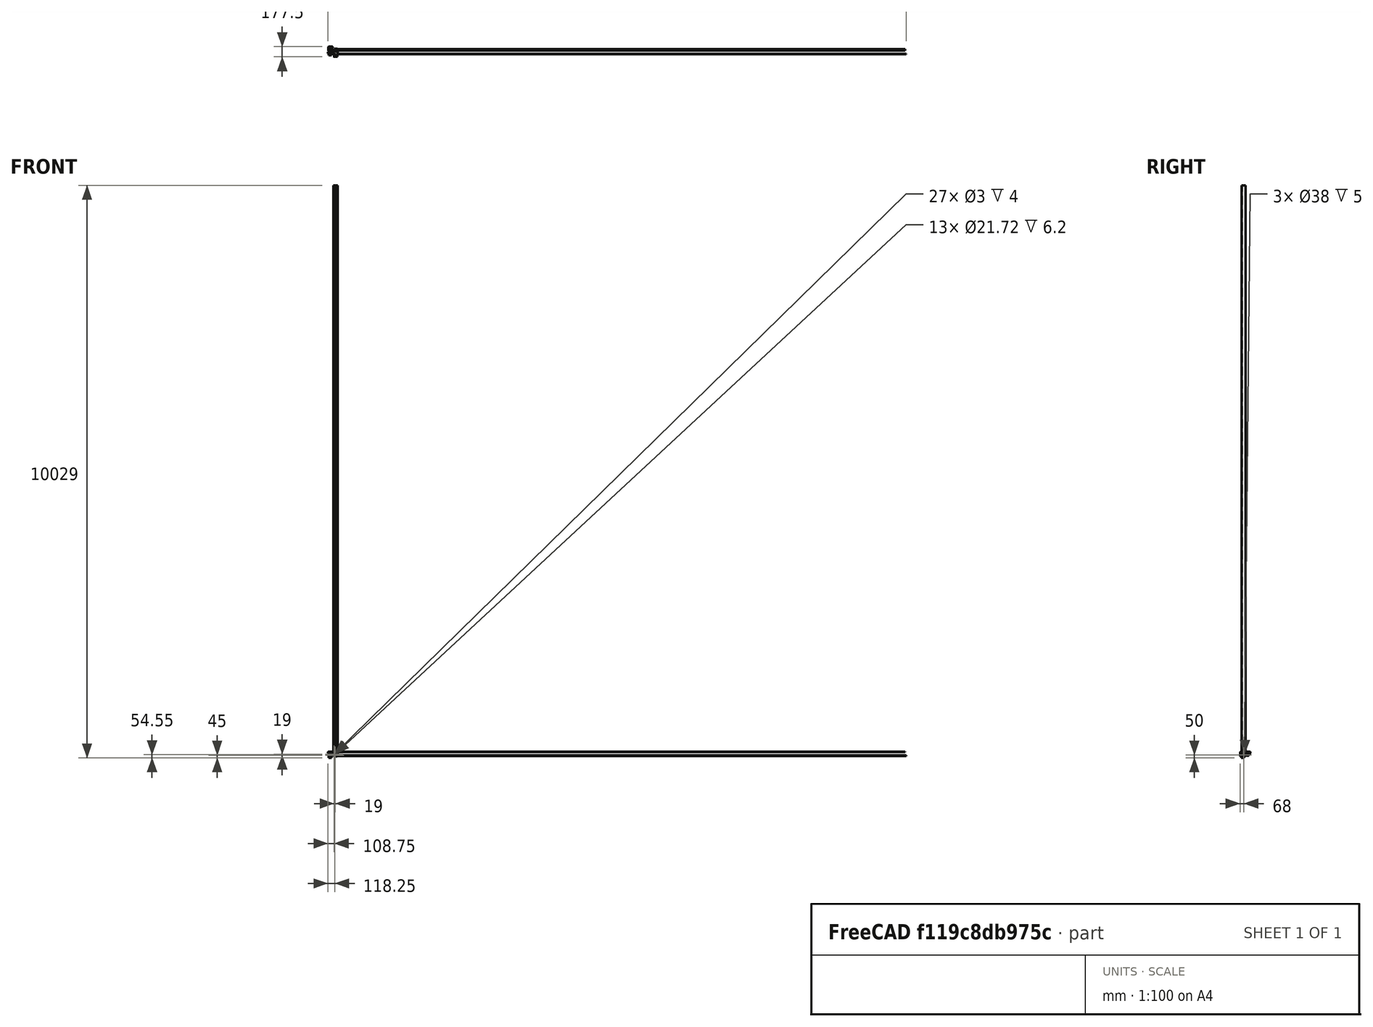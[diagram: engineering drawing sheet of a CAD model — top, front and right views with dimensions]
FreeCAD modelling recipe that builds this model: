
FCSTD DOCUMENT  (FreeCAD 0.15R4671 (Git))
Label: AllMetalJheadHotendFanShroud
License: All rights reserved
LicenseURL: http://en.wikipedia.org/wiki/All_rights_reserved
objects: Sketcher::SketchObject×30, Part::Feature×23, Mesh::Feature×22, PartDesign::Pocket×18, PartDesign::Pad×12, PartDesign::Fillet×10, Part::MultiFuse×1, PartDesign::Chamfer×1
note: 125 computed .brp shape members not serialized (recipe doc carries the construction recipe); baked Part::Feature solids carry a one-line shape summary decoded from their .brp

FEATURE [Part::Feature] Part__Feature  label="OB1515_45mm001"
  Placement = pos=(0,79.5,22.5) rot=(1,0,0;1.5708rad)
  shape: bbox 15 x 45 x 15 mm, 158 faces (baked)
FEATURE [Part::Feature] Part__Feature001  label="OB1515_45mm"
  Placement = pos=(7,93,-15) rot=(0,0,1;0.785398rad)
  shape: bbox 21.01 x 21.01 x 45 mm, 158 faces (baked)
FEATURE [Part::Feature] Part__Feature002  label="OB1515_45mm002"
  Placement = pos=(20.5,100,22.5) rot=(0.57735,0.57735,0.57735;2.0944rad)
  shape: bbox 45 x 15 x 15 mm, 158 faces (baked)
FEATURE [Part::Feature] Part__Feature003  label="NEMA17"
  Placement = pos=(36,64,2) rot=(0,0,1;0rad)
  shape: bbox 42.3 x 42.3 x 68 mm, 275 faces (baked)
FEATURE [Part::Feature] Part__Feature004  label="T5_Pulley"
  Placement = pos=(36,64,-4) rot=(0,0,1;0rad)
  shape: bbox 16 x 16 x 14.8 mm, 116 faces (baked)
FEATURE [Mesh::Feature] _08ZZ_Ball_Bearing  label="608ZZ_Ball_Bearing001"
  Placement = pos=(54.5,64,25.1) rot=(0,0,1;0rad)
FEATURE [Mesh::Feature] Spacer
  Placement = pos=(21.5,54,17.6) rot=(0,0,1;0rad)
FEATURE [Mesh::Feature] _mmRod_x100mm  label="8mmRod_x100mm"
  Placement = pos=(36,-64.5,-3.5) rot=(0,0,1;3.14159rad)
FEATURE [Part::Feature] Part__Feature005  label="TopCornerMotor"
  Placement = pos=(0,100,0) rot=(0,0,1;0rad)
  shape: bbox 69.55 x 77 x 28 mm, 82 faces (baked)
FEATURE [Part::Feature] Part__Feature006  label="TopRodHolder"
  Placement = pos=(0,100,2) rot=(0,0,1;0rad)
  shape: bbox 30.16 x 11.33 x 11.99 mm, 58 faces (baked)
FEATURE [Part::Feature] LM8UU_8mm_Linear_Bearing001
  Placement = pos=(36,-24.5,-3.5) rot=(0,0,1;1.5708rad)
  shape: bbox 15 x 24 x 15 mm, 34 faces (baked)
FEATURE [Mesh::Feature] _mmRod_x100mm001  label="8mmRod_x100mm001"
  Placement = pos=(66,7.5,1.5) rot=(0,0,1;1.5708rad)
FEATURE [Mesh::Feature] _mmRod_x100mm002  label="8mmRod_x100mm002"
  Placement = pos=(66,-32.5,1.5) rot=(0,0,1;1.5708rad)
FEATURE [Mesh::Feature] _0mmFan  label="40mmFan"
  Placement = pos=(102,-18,-36) rot=(-1,0,0;1.5708rad)
FEATURE [Mesh::Feature] HexHotEnd  label="HexHotEnd1"
  Placement = pos=(104,-57,-34) rot=(0,0,1;0rad)
FEATURE [Mesh::Feature] PNEUMATIC_NIPPLE
  Placement = pos=(111,-66,-3) rot=(0,-1,0;1.5708rad)
FEATURE [Part::Feature] Part__Feature015  label="AluAngle"
  Placement = pos=(0,5,-80) rot=(-1,0,0;1.5708rad)
  shape: bbox 50 x 50.8 x 50.8 mm, 9 faces (baked)
FEATURE [Mesh::Feature] _x10x4_FlangedBearing  label="5x10x4_FlangedBearing_BOTTOM"
  Placement = pos=(49,-6,16) rot=(-1,0,0;1.5708rad)
FEATURE [Mesh::Feature] _x10x4_FlangedBearing001  label="5x10x4_FlangedBearing_TOP"
  Placement = pos=(49,-6,12) rot=(1,0,0;1.5708rad)
FEATURE [Mesh::Feature] _x10x4_FlangedBearing002  label="5x10x4_FlangedBearing_BOTTOM001"
  Placement = pos=(49,-19,16) rot=(-1,0,0;1.5708rad)
FEATURE [Mesh::Feature] _x10x4_FlangedBearing003  label="5x10x4_FlangedBearing_TOP001"
  Placement = pos=(49,-19,12) rot=(1,0,0;1.5708rad)
FEATURE [Part::Feature] Part__Feature016  label="XCarrageBeltBlock"
  Placement = pos=(9,0,0) rot=(0,0,1;0rad)
  shape: bbox 56 x 22 x 10 mm, 113 faces (baked)
FEATURE [Part::Feature] Part__Feature017  label="LJ18A3"
  Placement = pos=(136,-57,-52) rot=(0,0,1;0rad)
  shape: bbox 17.85 x 17.85 x 79.1 mm, 11 faces (baked)
FEATURE [Mesh::Feature] HexNutStyle1_M002  label="HexNutStyle1_M006"
  Placement = pos=(50.3,7.15,-114) rot=(0,0,1;0.523599rad)
FEATURE [Mesh::Feature] HexNutStyle1_M003  label="HexNutStyle1_M007"
  Placement = pos=(50.3,20.15,-114) rot=(0,0,1;0.523599rad)
FEATURE [Part::Feature] Part__Feature018  label="YCarrage"
  shape: bbox 34.23 x 25.99 x 62.01 mm, 85 faces (baked)
FEATURE [Part::Feature] LM8UU_8mm_Linear_Bearing
  Placement = pos=(95,7.5,1.5) rot=(-1,0,0;1.5708rad)
  shape: bbox 24 x 15 x 15 mm, 34 faces (baked)
FEATURE [Part::Feature] LM8UU_8mm_Linear_Bearing002
  Placement = pos=(95,-32.5,1.5) rot=(-1,0,0;1.5708rad)
  shape: bbox 24 x 15 x 15 mm, 34 faces (baked)
FEATURE [Part::Feature] LM8UU_8mm_Linear_Bearing003
  Placement = pos=(123,7.5,1.5) rot=(-1,0,0;1.5708rad)
  shape: bbox 24 x 15 x 15 mm, 34 faces (baked)
FEATURE [Part::Feature] LM8UU_8mm_Linear_Bearing004
  Placement = pos=(123,-32.5,1.5) rot=(-1,0,0;1.5708rad)
  shape: bbox 24 x 15 x 15 mm, 34 faces (baked)
FEATURE [Mesh::Feature] MicroSwitch
  Placement = pos=(99,-12.5,-5) rot=(0,0,1;1.5708rad)
FEATURE [Part::Feature] Part__Feature019  label="XCarrageTop"
  shape: bbox 56 x 70.62 x 16.52 mm, 278 faces (baked)
FEATURE [Part::Feature] Part__Feature020  label="ChinaBlowerFan"
  shape: bbox 33.55 x 33.55 x 13 mm, 169 faces (baked)
FEATURE [Part::Feature] Part__Feature021  label="ChinaBlowerFan001"
  shape: bbox 40.62 x 40.6 x 19.6 mm, 81 faces (baked)
FEATURE [Part::MultiFuse] Fusion  label="ChinaBlowerFan002"
  Placement = pos=(114,-4,-13) rot=(0.707107,0.707107,0;3.14159rad)
  Shapes = -> [Part__Feature020,Part__Feature021]
FEATURE [Mesh::Feature] _0mmFan001  label="40mmFan001"
  Placement = pos=(141,-1,-23) rot=(0.57735,-0.57735,0.57735;4.18879rad)
FEATURE [Mesh::Feature] ALIEXPRESS_Aluhotend40mmFan
FEATURE [Mesh::Feature] Fan_25mm_x_10mm
  Placement = pos=(105.5,-31,-25.5) rot=(0,0.707107,0.707107;3.14159rad)
FEATURE [Mesh::Feature] HexHotEnd2
  Placement = pos=(104,-57,-34) rot=(0,0,1;0rad)
FEATURE [Part::Feature] Part__Feature022  label="Hexagon fanshroud"
  shape: bbox 25.5 x 25.5 x 18 mm, 35 faces (baked)
FEATURE [Mesh::Feature] hexagon_fan
  Placement = pos=(198.15,-46.7,56) rot=(0.57735,-0.57735,0.57735;2.0944rad)
FEATURE [Part::Feature] Part__Feature023  label="TempXCarrageBottom"
  shape: bbox 57.67 x 88 x 16.5 mm, 58 faces (baked)
FEATURE [Sketcher::SketchObject] Sketch
  Placement = pos=(0,0,-10.2) rot=(1,0,0;3.14159rad)
  sketch-geometry (4):
    g0: LineSegment StartX=93 StartY=70 StartZ=0 EndX=149 EndY=70 EndZ=0
    g1: LineSegment StartX=149 StartY=70 StartZ=0 EndX=149 EndY=-18 EndZ=0
    g2: LineSegment StartX=149 StartY=-18 StartZ=0 EndX=93 EndY=-18 EndZ=0
    g3: LineSegment StartX=93 StartY=-18 StartZ=0 EndX=93 EndY=70 EndZ=0
  constraints (8):
    c: Coincident(g0,g1)
    c: Coincident(g1,g2)
    c: Coincident(g2,g3)
    c: Coincident(g3,g0)
    c: Horizontal(g0)
    c: Horizontal(g2)
    c: Vertical(g1)
    c: Vertical(g3)
FEATURE [PartDesign::Pad] Pad
  Length = 3
  Length2 = 100
  Placement = pos=(0,0,-10.2) rot=(1,0,0;3.14159rad)
  Sketch = -> Sketch
  Type = 0
FEATURE [Sketcher::SketchObject] Sketch001
  Placement = pos=(0,0,-13.2) rot=(1,0,0;3.14159rad)
  Support = -> Pad [Face6]
  sketch-geometry (11):
    g0: LineSegment StartX=93 StartY=36 StartZ=0 EndX=118 EndY=36 EndZ=0
    g1: LineSegment StartX=118 StartY=36 StartZ=0 EndX=118 EndY=41 EndZ=0
    g2: LineSegment StartX=118 StartY=41 StartZ=0 EndX=114.5 EndY=62 EndZ=0
    g3: LineSegment StartX=93.5 StartY=62 StartZ=0 EndX=93 EndY=41 EndZ=0
    g4: LineSegment StartX=93 StartY=41 StartZ=0 EndX=93 EndY=36 EndZ=0
    g5: LineSegment StartX=114.5 StartY=62 StartZ=0 EndX=113 EndY=62 EndZ=0
    g6: LineSegment StartX=113 StartY=62 StartZ=0 EndX=113 EndY=52 EndZ=0
    g7: LineSegment StartX=113 StartY=52 StartZ=0 EndX=104 EndY=47 EndZ=0
    g8: LineSegment StartX=104 StartY=47 StartZ=0 EndX=95 EndY=52 EndZ=0
    g9: LineSegment StartX=95 StartY=52 StartZ=0 EndX=95 EndY=62 EndZ=0
    g10: LineSegment StartX=95 StartY=62 StartZ=0 EndX=93.5 EndY=62 EndZ=0
  constraints (16):
    c: Horizontal(g0)
    c: Coincident(g0,g1)
    c: Coincident(g1,g2)
    c: Coincident(g3,g4)
    c: Coincident(g4,g0)
    c: Coincident(g2,g5)
    c: Horizontal(g5)
    c: Coincident(g5,g6)
    c: Vertical(g6)
    c: Coincident(g6,g7)
    c: Coincident(g7,g8)
    c: Coincident(g8,g9)
    c: Vertical(g9)
    c: Coincident(g9,g10)
    c: Coincident(g10,g3)
    c: Horizontal(g10)
FEATURE [PartDesign::Pad] Pad001
  Length = 24.5
  Length2 = 100
  Placement = pos=(0,0,-10.2) rot=(1,0,0;3.14159rad)
  Sketch = -> Sketch001
  Type = 0
FEATURE [Sketcher::SketchObject] Sketch002
  Placement = pos=(93,0,-10.2) rot=(0.57735,0.57735,-0.57735;4.18879rad)
  Support = -> Pad001 [Face17]
  sketch-geometry (6):
    g0: LineSegment StartX=-63 StartY=23.5 StartZ=0 EndX=-62 EndY=23.5 EndZ=0
    g1: LineSegment StartX=-62 StartY=23.5 StartZ=0 EndX=-47 EndY=23.5 EndZ=0
    g2: LineSegment StartX=-47 StartY=23.5 StartZ=0 EndX=-41 EndY=25.5 EndZ=0
    g3: LineSegment StartX=-41 StartY=25.5 StartZ=0 EndX=-41 EndY=28 EndZ=0
    g4: LineSegment StartX=-41 StartY=28 StartZ=0 EndX=-63 EndY=28 EndZ=0
    g5: LineSegment StartX=-63 StartY=28 StartZ=0 EndX=-63 EndY=23.5 EndZ=0
  constraints (11):
    c: Horizontal(g0)
    c: Coincident(g0,g1)
    c: Horizontal(g1)
    c: Coincident(g1,g2)
    c: Coincident(g2,g3)
    c: Vertical(g3)
    c: Coincident(g3,g4)
    c: Horizontal(g4)
    c: Coincident(g4,g5)
    c: Coincident(g5,g0)
    c: Vertical(g5)
FEATURE [PartDesign::Pocket] Pocket
  Length = 5
  Placement = pos=(0,0,-10.2) rot=(1,0,0;3.14159rad)
  Sketch = -> Sketch002
  Type = 1
FEATURE [Sketcher::SketchObject] Sketch003
  Placement = pos=(0,-36,-10.2) rot=(-1,0,0;1.5708rad)
  Support = -> Pocket [Face7]
  sketch-geometry (1):
    g0: Circle CenterX=105.5 CenterY=15.25 CenterZ=0 NormalX=0 NormalY=0 NormalZ=1 Radius=10.8605
FEATURE [PartDesign::Pocket] Pocket001
  Length = 3
  Placement = pos=(0,0,-10.2) rot=(1,0,0;3.14159rad)
  Sketch = -> Sketch003
  Type = 0
FEATURE [Sketcher::SketchObject] Sketch004
  Placement = pos=(0,0,-10.2) rot=(0,0,1;0rad)
  Support = -> Pocket001 [Face4]
  sketch-geometry (7):
    g0: LineSegment StartX=94.75 StartY=-70.5 StartZ=0 EndX=94.75 EndY=-38.75 EndZ=0
    g1: LineSegment StartX=94.75 StartY=-38.75 StartZ=0 EndX=116.25 EndY=-38.75 EndZ=0
    g2: LineSegment StartX=116.25 StartY=-38.75 StartZ=0 EndX=116.5 EndY=-39 EndZ=0
    g3: LineSegment StartX=116.5 StartY=-39 StartZ=0 EndX=116.5 EndY=-41 EndZ=0
    g4: LineSegment StartX=116.5 StartY=-41 StartZ=0 EndX=113 EndY=-62 EndZ=0
    g5: LineSegment StartX=113 StartY=-62 StartZ=0 EndX=113 EndY=-70.5 EndZ=0
    g6: LineSegment StartX=113 StartY=-70.5 StartZ=0 EndX=94.75 EndY=-70.5 EndZ=0
  constraints (12):
    c: Vertical(g0)
    c: Horizontal(g1)
    c: Coincident(g1,g2)
    c: Coincident(g2,g3)
    c: Vertical(g3)
    c: Coincident(g3,g4)
    c: Coincident(g4,g5)
    c: Vertical(g5)
    c: Coincident(g5,g6)
    c: Horizontal(g6)
    c: Coincident(g0,g6)
    c: Coincident(g0,g1)
FEATURE [PartDesign::Pocket] Pocket002
  Length = 22.8
  Placement = pos=(0,0,-10.2) rot=(1,0,0;3.14159rad)
  Sketch = -> Sketch004
  Type = 0
FEATURE [PartDesign::Chamfer] Chamfer
  Base = -> Pocket002 [Edge60]
  Placement = pos=(0,0,-10.2) rot=(1,0,0;3.14159rad)
  Size = 3.2
FEATURE [PartDesign::Fillet] Fillet
  Base = -> Chamfer [Edge86,Edge76]
  Placement = pos=(0,0,-10.2) rot=(1,0,0;3.14159rad)
  Radius = 2
FEATURE [Sketcher::SketchObject] Sketch005
  Placement = pos=(0,0,-13.2) rot=(1,0,0;3.14159rad)
  Support = -> Fillet [Face4]
  sketch-geometry (8):
    g0: LineSegment StartX=92.5 StartY=41 StartZ=0 EndX=93.5 EndY=41 EndZ=0
    g1: LineSegment StartX=93.5 StartY=41 StartZ=0 EndX=93.5 EndY=62 EndZ=0
    g2: LineSegment StartX=93.5 StartY=62 StartZ=0 EndX=114.5 EndY=62 EndZ=0
    g3: LineSegment StartX=114.5 StartY=62 StartZ=0 EndX=118 EndY=41 EndZ=0
    g4: LineSegment StartX=118 StartY=41 StartZ=0 EndX=149.5 EndY=41 EndZ=0
    g5: LineSegment StartX=149.5 StartY=41 StartZ=0 EndX=149.5 EndY=70.25 EndZ=0
    g6: LineSegment StartX=149.5 StartY=70.25 StartZ=0 EndX=92.5 EndY=70.25 EndZ=0
    g7: LineSegment StartX=92.5 StartY=70.25 StartZ=0 EndX=92.5 EndY=41 EndZ=0
  constraints (14):
    c: Horizontal(g0)
    c: Coincident(g0,g1)
    c: Vertical(g1)
    c: Coincident(g1,g2)
    c: Horizontal(g2)
    c: Coincident(g2,g3)
    c: Coincident(g3,g4)
    c: Horizontal(g4)
    c: Coincident(g4,g5)
    c: Vertical(g5)
    c: Coincident(g5,g6)
    c: Horizontal(g6)
    c: Coincident(g6,g7)
    c: Coincident(g7,g0)
FEATURE [PartDesign::Pocket] Pocket003
  Length = 5
  Placement = pos=(0,0,-10.2) rot=(1,0,0;3.14159rad)
  Sketch = -> Sketch005
  Type = 0
FEATURE [Sketcher::SketchObject] Sketch006
  Placement = pos=(0,0,-10.2) rot=(0,0,1;0rad)
  Support = -> Pocket003 [Face11]
  sketch-geometry (7):
    g0: LineSegment StartX=93 StartY=-38.25 StartZ=0 EndX=93 EndY=-41 EndZ=0
    g1: LineSegment StartX=93 StartY=-41 StartZ=0 EndX=93.5 EndY=-62 EndZ=0
    g2: LineSegment StartX=93.5 StartY=-62 StartZ=0 EndX=94 EndY=-62 EndZ=0
    g3: LineSegment StartX=94 StartY=-62 StartZ=0 EndX=94 EndY=-44.25 EndZ=0
    g4: LineSegment StartX=94 StartY=-44.25 StartZ=0 EndX=116.75 EndY=-44.25 EndZ=0
    g5: LineSegment StartX=116.75 StartY=-44.25 StartZ=0 EndX=116.75 EndY=-38.25 EndZ=0
    g6: LineSegment StartX=116.75 StartY=-38.25 StartZ=0 EndX=93 EndY=-38.25 EndZ=0
  constraints (12):
    c: Vertical(g0)
    c: Coincident(g0,g1)
    c: Coincident(g1,g2)
    c: Horizontal(g2)
    c: Coincident(g2,g3)
    c: Coincident(g3,g4)
    c: Horizontal(g4)
    c: Coincident(g4,g5)
    c: Vertical(g5)
    c: Coincident(g5,g6)
    c: Horizontal(g6)
    c: Coincident(g0,g6)
FEATURE [PartDesign::Pad] Pad002
  Length = 3
  Length2 = 100
  Placement = pos=(0,0,-10.2) rot=(1,0,0;3.14159rad)
  Reversed = true
  Sketch = -> Sketch006
  Type = 0
FEATURE [Part::Feature] Pad002001  label="Pad003"
  shape: bbox 56 x 80 x 27.5 mm, 37 faces (baked)
FEATURE [Sketcher::SketchObject] Sketch007
  Placement = pos=(0,0,-13.2) rot=(1,0,0;3.14159rad)
  Support = -> Pad002001 [Face32]
  sketch-geometry (2):
    g0: Circle CenterX=107 CenterY=44.25 CenterZ=0 NormalX=0 NormalY=0 NormalZ=1 Radius=1.8
    g1: Circle CenterX=107 CenterY=44.25 CenterZ=0 NormalX=0 NormalY=0 NormalZ=1 Radius=3.25
  constraints (2):
    c: Radius(g0) = 1.8
    c: Coincident(g1,g0)
FEATURE [PartDesign::Pad] Pad002002
  Length = 3
  Length2 = 100
  Reversed = true
  Sketch = -> Sketch007
  Type = 0
FEATURE [Sketcher::SketchObject] Sketch008
  Placement = pos=(0,0,-13.2) rot=(1,0,0;3.14159rad)
  Support = -> Pad002002 [Face38]
  sketch-geometry (1):
    g0: Circle CenterX=107 CenterY=44.25 CenterZ=0 NormalX=0 NormalY=0 NormalZ=1 Radius=1.81
  constraints (1):
    c: Radius(g0) = 1.81
FEATURE [PartDesign::Pocket] Pocket004
  Length = 4
  Sketch = -> Sketch008
  Type = 0
FEATURE [PartDesign::Fillet] Fillet001
  Base = -> Pocket004 [Edge109,Edge105]
  Radius = 3
FEATURE [PartDesign::Fillet] Fillet002
  Base = -> Fillet001 [Edge42,Edge20]
  Radius = 2
FEATURE [Sketcher::SketchObject] Sketch009
  Placement = pos=(0,-36,0) rot=(0,0.707107,0.707107;3.14159rad)
  Support = -> Fillet002 [Face34]
  sketch-geometry (4):
    g0: Circle CenterX=-115 CenterY=-16 CenterZ=0 NormalX=0 NormalY=0 NormalZ=1 Radius=1.5
    g1: Circle CenterX=-96 CenterY=-16 CenterZ=0 NormalX=0 NormalY=0 NormalZ=1 Radius=1.5
    g2: Circle CenterX=-96 CenterY=-35 CenterZ=0 NormalX=0 NormalY=0 NormalZ=1 Radius=1.5
    g3: Circle CenterX=-115 CenterY=-35 CenterZ=0 NormalX=0 NormalY=0 NormalZ=1 Radius=1.5
  constraints (4):
    c: Radius(g0) = 1.5
    c: Radius(g1) = 1.5
    c: Radius(g2) = 1.5
    c: Radius(g3) = 1.5
FEATURE [PartDesign::Pocket] Pocket005
  Length = 4
  Sketch = -> Sketch009
  Type = 0
FEATURE [Sketcher::SketchObject] Sketch011
  Placement = pos=(0,0,-13.2) rot=(1,0,0;3.14159rad)
  Support = -> Pocket005 [Face27]
  sketch-geometry (4):
    g0: LineSegment StartX=138 StartY=-18 StartZ=0 EndX=134 EndY=-18 EndZ=0
    g1: LineSegment StartX=134 StartY=-18 StartZ=0 EndX=134 EndY=22 EndZ=0
    g2: LineSegment StartX=134 StartY=22 StartZ=0 EndX=138 EndY=22 EndZ=0
    g3: LineSegment StartX=138 StartY=22 StartZ=0 EndX=138 EndY=-18 EndZ=0
  constraints (8):
    c: Coincident(g0,g1)
    c: Coincident(g1,g2)
    c: Coincident(g2,g3)
    c: Coincident(g3,g0)
    c: Horizontal(g0)
    c: Horizontal(g2)
    c: Vertical(g1)
    c: Vertical(g3)
FEATURE [PartDesign::Pad] Pad002003
  Length = 37
  Length2 = 100
  Sketch = -> Sketch011
  Type = 0
FEATURE [Sketcher::SketchObject] Sketch012
  Placement = pos=(138,0,0) rot=(0.57735,0.57735,0.57735;2.0944rad)
  Support = -> Pad002003 [Face45]
  sketch-geometry (1):
    g0: Circle CenterX=-2 CenterY=-30 CenterZ=0 NormalX=0 NormalY=0 NormalZ=1 Radius=19
  constraints (1):
    c: Radius(g0) = 19
FEATURE [PartDesign::Pocket] Pocket006
  Length = 5
  Sketch = -> Sketch012
  Type = 0
FEATURE [Sketcher::SketchObject] Sketch013
  Placement = pos=(0,18,0) rot=(0,0.707107,0.707107;3.14159rad)
  Support = -> Pocket006 [Face15]
  sketch-geometry (6):
    g0: LineSegment StartX=-135 StartY=-50 StartZ=0 EndX=-93 EndY=-50 EndZ=0
    g1: LineSegment StartX=-93 StartY=-50 StartZ=0 EndX=-93 EndY=-39 EndZ=0
    g2: LineSegment StartX=-135 StartY=-12 StartZ=0 EndX=-135 EndY=-50 EndZ=0
    g3: LineSegment StartX=-93 StartY=-39 StartZ=0 EndX=-120 EndY=-39 EndZ=0
    g4: LineSegment StartX=-120 StartY=-39 StartZ=0 EndX=-126 EndY=-12 EndZ=0
    g5: LineSegment StartX=-126 StartY=-12 StartZ=0 EndX=-135 EndY=-12 EndZ=0
  constraints (11):
    c: Coincident(g0,g1)
    c: Coincident(g2,g0)
    c: Horizontal(g0)
    c: Vertical(g1)
    c: Vertical(g2)
    c: Coincident(g1,g3)
    c: Horizontal(g3)
    c: Coincident(g3,g4)
    c: Coincident(g4,g5)
    c: Horizontal(g5)
    c: Coincident(g2,g5)
FEATURE [PartDesign::Pad] Pad002004
  Length = 40
  Length2 = 100
  Reversed = true
  Sketch = -> Sketch013
  Type = 0
FEATURE [Sketcher::SketchObject] Sketch014
  Placement = pos=(93,0,0) rot=(0.57735,-0.57735,-0.57735;2.0944rad)
  Support = -> Pad002004 [Face57]
  sketch-geometry (5):
    g0: LineSegment StartX=24 StartY=-51.2126 StartZ=0 EndX=24 EndY=-41 EndZ=0
    g1: LineSegment StartX=24 StartY=-41 StartZ=0 EndX=22 EndY=-41 EndZ=0
    g2: LineSegment StartX=22 StartY=-41 StartZ=0 EndX=17 EndY=-50.2195 EndZ=0
    g3: LineSegment StartX=17 StartY=-50.2195 StartZ=0 EndX=17 EndY=-51.2126 EndZ=0
    g4: LineSegment StartX=17 StartY=-51.2126 StartZ=0 EndX=24 EndY=-51.2126 EndZ=0
  constraints (9):
    c: Vertical(g0)
    c: Coincident(g0,g1)
    c: Horizontal(g1)
    c: Coincident(g1,g2)
    c: Coincident(g2,g3)
    c: Vertical(g3)
    c: Coincident(g3,g4)
    c: Coincident(g4,g0)
    c: Horizontal(g4)
FEATURE [PartDesign::Pocket] Pocket007
  Length = 5
  Sketch = -> Sketch014
  Type = 1
FEATURE [PartDesign::Fillet] Fillet003
  Base = -> Pocket007 [Edge73]
  Radius = 25
FEATURE [Sketcher::SketchObject] Sketch015
  Placement = pos=(93,0,0) rot=(0.57735,-0.57735,-0.57735;2.0944rad)
  Support = -> Fillet003 [Face13]
  sketch-geometry (4):
    g0: LineSegment StartX=-21.7137 StartY=-49 StartZ=0 EndX=26 EndY=-49 EndZ=0
    g1: LineSegment StartX=26 StartY=-49 StartZ=0 EndX=26 EndY=-52 EndZ=0
    g2: LineSegment StartX=26 StartY=-52 StartZ=0 EndX=-21.7137 EndY=-52 EndZ=0
    g3: LineSegment StartX=-21.7137 StartY=-52 StartZ=0 EndX=-21.7137 EndY=-49 EndZ=0
  constraints (8):
    c: Coincident(g0,g1)
    c: Coincident(g1,g2)
    c: Coincident(g2,g3)
    c: Coincident(g3,g0)
    c: Horizontal(g0)
    c: Horizontal(g2)
    c: Vertical(g1)
    c: Vertical(g3)
FEATURE [PartDesign::Pocket] Pocket008
  Length = 41
  Sketch = -> Sketch015
  Type = 0
FEATURE [Sketcher::SketchObject] Sketch016
  Placement = pos=(0,0,-49) rot=(1,0,0;3.14159rad)
  Support = -> Pocket008 [Face2]
  sketch-geometry (5):
    g0: ArcOfCircle CenterX=117.001 CenterY=6 CenterZ=0 NormalX=0 NormalY=0 NormalZ=1 Radius=21.0014 StartAngle=3.14159 EndAngle=4.72394
    g1: LineSegment StartX=96 StartY=6 StartZ=0 EndX=96 EndY=23.1942 EndZ=0
    g2: LineSegment StartX=96 StartY=23.1942 StartZ=0 EndX=134 EndY=23.1942 EndZ=0
    g3: LineSegment StartX=134 StartY=23.1942 StartZ=0 EndX=134 EndY=-15 EndZ=0
    g4: LineSegment StartX=134 StartY=-15 StartZ=0 EndX=117.244 EndY=-15 EndZ=0
  constraints (8):
    c: Tangent(g0,g1) = 1.5708
    c: Coincident(g1,g2)
    c: Horizontal(g2)
    c: Coincident(g2,g3)
    c: Vertical(g3)
    c: Coincident(g3,g4)
    c: Coincident(g4,g0)
    c: Horizontal(g4)
FEATURE [PartDesign::Pocket] Pocket009
  Length = 8
  Sketch = -> Sketch016
  Type = 0
FEATURE [Sketcher::SketchObject] Sketch017
  Placement = pos=(0,-22,0) rot=(1,0,0;1.5708rad)
  Support = -> Pocket009 [Face18]
  sketch-geometry (5):
    g0: LineSegment StartX=134 StartY=-13 StartZ=0 EndX=128 EndY=-13 EndZ=0
    g1: LineSegment StartX=128 StartY=-13 StartZ=0 EndX=122 EndY=-41 EndZ=0
    g2: LineSegment StartX=122 StartY=-41 StartZ=0 EndX=122 EndY=-42 EndZ=0
    g3: LineSegment StartX=122 StartY=-42 StartZ=0 EndX=134 EndY=-42 EndZ=0
    g4: LineSegment StartX=134 StartY=-42 StartZ=0 EndX=134 EndY=-13 EndZ=0
  constraints (7):
    c: Coincident(g0,g1)
    c: Coincident(g1,g2)
    c: Coincident(g2,g3)
    c: Horizontal(g3)
    c: Coincident(g3,g4)
    c: Vertical(g4)
    c: Coincident(g0,g4)
FEATURE [PartDesign::Pocket] Pocket010
  Length = 37
  Sketch = -> Sketch017
  Type = 0
FEATURE [PartDesign::Fillet] Fillet004
  Base = -> Pocket010 [Edge164]
  Radius = 6
FEATURE [PartDesign::Fillet] Fillet005
  Base = -> Fillet004 [Edge42]
  Radius = 4
FEATURE [PartDesign::Fillet] Fillet006
  Base = -> Fillet005 [Edge10]
  Radius = 3
FEATURE [Sketcher::SketchObject] Sketch018
  Placement = pos=(149,0,0) rot=(0.57735,0.57735,0.57735;2.0944rad)
  Support = -> Fillet006 [Face30]
  sketch-geometry (1):
    g0: Circle CenterX=-2 CenterY=-30 CenterZ=0 NormalX=0 NormalY=0 NormalZ=1 Radius=19.1
  constraints (1):
    c: Radius(g0) = 19.1
FEATURE [PartDesign::Pocket] Pocket011
  Length = 15
  Sketch = -> Sketch018
  Type = 0
FEATURE [Sketcher::SketchObject] Sketch019
  Placement = pos=(0,0,-49) rot=(1,0,0;3.14159rad)
  Support = -> Pocket011 [Face15]
  sketch-geometry (5):
    g0: LineSegment StartX=93 StartY=17.75 StartZ=0 EndX=138 EndY=17.75 EndZ=0
    g1: LineSegment StartX=138 StartY=17.75 StartZ=0 EndX=138 EndY=-18.0159 EndZ=0
    g2: LineSegment StartX=138 StartY=-18.0159 StartZ=0 EndX=117.75 EndY=-18.0159 EndZ=0
    g3: LineSegment StartX=93 StartY=17.75 StartZ=0 EndX=93 EndY=6.75 EndZ=0
    g4: ArcOfCircle CenterX=117.884 CenterY=6.86846 CenterZ=0 NormalX=0 NormalY=0 NormalZ=1 Radius=24.8847 StartAngle=3.14635 EndAngle=4.70698
  constraints (9):
    c: Horizontal(g0)
    c: Coincident(g0,g1)
    c: Vertical(g1)
    c: Coincident(g1,g2)
    c: Horizontal(g2)
    c: Coincident(g3,g0)
    c: Vertical(g3)
    c: Coincident(g4,g2)
    c: Coincident(g4,g3)
FEATURE [PartDesign::Pad] Pad002005
  Length = 2
  Length2 = 100
  Sketch = -> Sketch019
  Type = 0
FEATURE [Sketcher::SketchObject] Sketch020
  Placement = pos=(93,0,0) rot=(0.57735,-0.57735,-0.57735;2.0944rad)
  Support = -> Pad002005 [Face90]
  sketch-geometry (5):
    g0: LineSegment StartX=22.25 StartY=-39 StartZ=0 EndX=22 EndY=-39 EndZ=0
    g1: LineSegment StartX=22 StartY=-39 StartZ=0 EndX=17.5 EndY=-49 EndZ=0
    g2: LineSegment StartX=17.5 StartY=-49 StartZ=0 EndX=17.5 EndY=-51 EndZ=0
    g3: LineSegment StartX=17.5 StartY=-51 StartZ=0 EndX=22.25 EndY=-51 EndZ=0
    g4: LineSegment StartX=22.25 StartY=-51 StartZ=0 EndX=22.25 EndY=-39 EndZ=0
  constraints (9):
    c: Horizontal(g0)
    c: Coincident(g0,g1)
    c: Coincident(g1,g2)
    c: Vertical(g2)
    c: Coincident(g2,g3)
    c: Horizontal(g3)
    c: Coincident(g3,g4)
    c: Coincident(g4,g0)
    c: Vertical(g4)
FEATURE [Sketcher::SketchObject] Sketch021
  Placement = pos=(0,-22,0) rot=(1,0,0;1.5708rad)
  Support = -> Pad002005 [Face26]
  sketch-geometry (6):
    g0: LineSegment StartX=138 StartY=-13 StartZ=0 EndX=125.75 EndY=-13 EndZ=0
    g1: LineSegment StartX=125.75 StartY=-13 StartZ=0 EndX=120 EndY=-39 EndZ=0
    g2: LineSegment StartX=120 StartY=-39 StartZ=0 EndX=112 EndY=-39 EndZ=0
    g3: LineSegment StartX=112 StartY=-39 StartZ=0 EndX=112 EndY=-51 EndZ=0
    g4: LineSegment StartX=112 StartY=-51 StartZ=0 EndX=138 EndY=-51 EndZ=0
    g5: LineSegment StartX=138 StartY=-51 StartZ=0 EndX=138 EndY=-13 EndZ=0
  constraints (11):
    c: Horizontal(g0)
    c: Coincident(g0,g1)
    c: Coincident(g1,g2)
    c: Horizontal(g2)
    c: Coincident(g2,g3)
    c: Vertical(g3)
    c: Coincident(g3,g4)
    c: Horizontal(g4)
    c: Coincident(g4,g5)
    c: Coincident(g5,g0)
    c: Vertical(g5)
FEATURE [PartDesign::Pad] Pad002006
  Length = 3
  Length2 = 100
  Sketch = -> Sketch021
  Type = 0
FEATURE [PartDesign::Pad] Pad002007
  Length = 45
  Length2 = 100
  Reversed = true
  Sketch = -> Sketch020
  Type = 0
FEATURE [Sketcher::SketchObject] Sketch022
  Placement = pos=(93,0,0) rot=(0.57735,-0.57735,-0.57735;2.0944rad)
  Support = -> Pad002007 [Face90]
  sketch-geometry (4):
    g0: LineSegment StartX=26 StartY=-52 StartZ=0 EndX=16.1404 EndY=-52 EndZ=0
    g1: LineSegment StartX=16.1404 StartY=-52 StartZ=0 EndX=22 EndY=-39 EndZ=0
    g2: LineSegment StartX=22 StartY=-39 StartZ=0 EndX=26 EndY=-39 EndZ=0
    g3: LineSegment StartX=26 StartY=-39 StartZ=0 EndX=26 EndY=-52 EndZ=0
  constraints (7):
    c: Horizontal(g0)
    c: Coincident(g0,g1)
    c: Coincident(g1,g2)
    c: Horizontal(g2)
    c: Coincident(g2,g3)
    c: Coincident(g3,g0)
    c: Vertical(g3)
FEATURE [Sketcher::SketchObject] Sketch023
  Placement = pos=(0,-22.25,0) rot=(1,0,0;1.5708rad)
  Support = -> Pad002007 [Face1]
  sketch-geometry (4):
    g0: LineSegment StartX=138 StartY=-39.25 StartZ=0 EndX=138 EndY=-13 EndZ=0
    g1: LineSegment StartX=138 StartY=-13 StartZ=0 EndX=125.75 EndY=-13 EndZ=0
    g2: LineSegment StartX=125.75 StartY=-13 StartZ=0 EndX=120 EndY=-39.25 EndZ=0
    g3: LineSegment StartX=120 StartY=-39.25 StartZ=0 EndX=138 EndY=-39.25 EndZ=0
  constraints (7):
    c: Vertical(g0)
    c: Coincident(g0,g1)
    c: Horizontal(g1)
    c: Coincident(g1,g2)
    c: Coincident(g2,g3)
    c: PointOnObject(g3,g0)
    c: Horizontal(g3)
FEATURE [PartDesign::Pad] Pad002008
  Length = 2
  Length2 = 100
  Reversed = true
  Sketch = -> Sketch023
  Type = 0
FEATURE [PartDesign::Pocket] Pocket012
  Length = 19
  Sketch = -> Sketch022
  Type = 0
FEATURE [Sketcher::SketchObject] Sketch024
  Placement = pos=(112,0,0) rot=(0.57735,-0.57735,-0.57735;2.0944rad)
  Support = -> Pocket012 [Face2]
  sketch-geometry (6):
    g0: LineSegment StartX=22.75 StartY=-38.5 StartZ=0 EndX=22 EndY=-38.5 EndZ=0
    g1: LineSegment StartX=22 StartY=-38.5 StartZ=0 EndX=22 EndY=-42 EndZ=0
    g2: LineSegment StartX=22 StartY=-42 StartZ=0 EndX=18.25 EndY=-51.25 EndZ=0
    g3: LineSegment StartX=18.25 StartY=-51.25 StartZ=0 EndX=18.25 EndY=-51.75 EndZ=0
    g4: LineSegment StartX=18.25 StartY=-51.75 StartZ=0 EndX=22.75 EndY=-51.75 EndZ=0
    g5: LineSegment StartX=22.75 StartY=-51.75 StartZ=0 EndX=22.75 EndY=-38.5 EndZ=0
  constraints (11):
    c: Horizontal(g0)
    c: Coincident(g0,g1)
    c: Vertical(g1)
    c: Coincident(g1,g2)
    c: Coincident(g2,g3)
    c: Vertical(g3)
    c: Coincident(g3,g4)
    c: Horizontal(g4)
    c: Coincident(g4,g5)
    c: Coincident(g5,g0)
    c: Vertical(g5)
FEATURE [PartDesign::Pocket] Pocket013
  Length = 5
  Sketch = -> Sketch024
  Type = 1
FEATURE [Sketcher::SketchObject] Sketch025
  Placement = pos=(138,0,0) rot=(0.57735,0.57735,0.57735;2.0944rad)
  Support = -> Pocket013 [Face14]
  sketch-geometry (4):
    g0: LineSegment StartX=-22 StartY=-40 StartZ=0 EndX=-21 EndY=-40 EndZ=0
    g1: LineSegment StartX=-21 StartY=-40 StartZ=0 EndX=-21 EndY=-12.92 EndZ=0
    g2: LineSegment StartX=-21 StartY=-12.92 StartZ=0 EndX=-22 EndY=-12.92 EndZ=0
    g3: LineSegment StartX=-22 StartY=-12.92 StartZ=0 EndX=-22 EndY=-40 EndZ=0
  constraints (8):
    c: Coincident(g0,g1)
    c: Coincident(g1,g2)
    c: Coincident(g2,g3)
    c: Coincident(g3,g0)
    c: Horizontal(g0)
    c: Horizontal(g2)
    c: Vertical(g1)
    c: Vertical(g3)
FEATURE [PartDesign::Pad] Pad002009
  Length = 22
  Length2 = 100
  Reversed = true
  Sketch = -> Sketch025
  Type = 0
FEATURE [Sketcher::SketchObject] Sketch026
  Placement = pos=(0,-21,0) rot=(0,0.707107,0.707107;3.14159rad)
  Support = -> Pad002009 [Face27]
  sketch-geometry (11):
    g0: LineSegment StartX=-115.74 StartY=-13.2067 StartZ=0 EndX=-125.75 EndY=-13.2067 EndZ=0
    g1: LineSegment StartX=-125.75 StartY=-13.2067 StartZ=0 EndX=-120.679 EndY=-35.8838 EndZ=0
    g2: LineSegment StartX=-120.679 StartY=-35.8838 StartZ=0 EndX=-120.25 EndY=-36.9498 EndZ=0
    g3: LineSegment StartX=-120.25 StartY=-36.9498 StartZ=0 EndX=-119.584 EndY=-37.843 EndZ=0
    g4: LineSegment StartX=-119.584 StartY=-37.843 StartZ=0 EndX=-118.75 EndY=-38.448 EndZ=0
    g5: LineSegment StartX=-118.75 StartY=-38.448 StartZ=0 EndX=-118.375 EndY=-38.6372 EndZ=0
    g6: LineSegment StartX=-118.375 StartY=-38.6372 StartZ=0 EndX=-117.599 EndY=-38.8897 EndZ=0
    g7: LineSegment StartX=-117.599 StartY=-38.8897 StartZ=0 EndX=-117.25 EndY=-38.935 EndZ=0
    g8: LineSegment StartX=-117.25 StartY=-38.935 StartZ=0 EndX=-116.75 EndY=-39 EndZ=0
    g9: LineSegment StartX=-116.75 StartY=-39 StartZ=0 EndX=-115.74 EndY=-39 EndZ=0
    g10: LineSegment StartX=-115.74 StartY=-39 StartZ=0 EndX=-115.74 EndY=-13.2067 EndZ=0
  constraints (14):
    c: Horizontal(g0)
    c: Coincident(g0,g1)
    c: Coincident(g1,g2)
    c: Coincident(g2,g3)
    c: Coincident(g3,g4)
    c: Coincident(g4,g5)
    c: Coincident(g5,g6)
    c: Coincident(g6,g7)
    c: Coincident(g7,g8)
    c: Coincident(g8,g9)
    c: Horizontal(g9)
    c: Coincident(g9,g10)
    c: Coincident(g10,g0)
    c: Vertical(g10)
FEATURE [PartDesign::Pocket] Pocket014
  Length = 5
  Sketch = -> Sketch026
  Type = 0
FEATURE [Sketcher::SketchObject] Sketch027
  Placement = pos=(0,0,-13.2) rot=(1,0,0;3.14159rad)
  Support = -> Pocket014 [Face42]
  sketch-geometry (4):
    g0: LineSegment StartX=150 StartY=22 StartZ=0 EndX=138 EndY=22 EndZ=0
    g1: LineSegment StartX=138 StartY=22 StartZ=0 EndX=138 EndY=-19 EndZ=0
    g2: LineSegment StartX=138 StartY=-19 StartZ=0 EndX=150 EndY=-19 EndZ=0
    g3: LineSegment StartX=150 StartY=-19 StartZ=0 EndX=150 EndY=22 EndZ=0
  constraints (8):
    c: Coincident(g0,g1)
    c: Coincident(g1,g2)
    c: Coincident(g2,g3)
    c: Coincident(g3,g0)
    c: Horizontal(g0)
    c: Horizontal(g2)
    c: Vertical(g1)
    c: Vertical(g3)
FEATURE [PartDesign::Pocket] Pocket015
  Length = 5
  Sketch = -> Sketch027
  Type = 0
FEATURE [Sketcher::SketchObject] Sketch028
  Placement = pos=(0,0,-51) rot=(1,0,0;3.14159rad)
  Support = -> Pocket015 [Face8]
  sketch-geometry (6):
    g0: LineSegment StartX=118 StartY=22 StartZ=0 EndX=118 EndY=42 EndZ=0
    g1: LineSegment StartX=118 StartY=42 StartZ=0 EndX=157.22 EndY=42 EndZ=0
    g2: LineSegment StartX=157.22 StartY=42 StartZ=0 EndX=157.22 EndY=-28.296 EndZ=0
    g3: LineSegment StartX=157.22 StartY=-28.296 StartZ=0 EndX=78.471 EndY=-28.296 EndZ=0
    g4: LineSegment StartX=78.471 StartY=-28.296 StartZ=0 EndX=78.471 EndY=22 EndZ=0
    g5: LineSegment StartX=78.471 StartY=22 StartZ=0 EndX=118 EndY=22 EndZ=0
  constraints (11):
    c: Vertical(g0)
    c: Coincident(g0,g1)
    c: Horizontal(g1)
    c: Coincident(g1,g2)
    c: Vertical(g2)
    c: Coincident(g2,g3)
    c: Horizontal(g3)
    c: Coincident(g3,g4)
    c: Vertical(g4)
    c: Coincident(g4,g5)
    c: Horizontal(g5)
FEATURE [PartDesign::Pocket] Pocket016
  Length = 5
  Sketch = -> Sketch028
  Type = 1
FEATURE [Sketcher::SketchObject] Sketch029
  Placement = pos=(0,0,-13.2) rot=(1,0,0;3.14159rad)
  Support = -> Pocket016 [Face24]
  sketch-geometry (2):
    g0: Circle CenterX=96.46 CenterY=22 CenterZ=0 NormalX=0 NormalY=0 NormalZ=1 Radius=3.46164
    g1: Circle CenterX=114.5 CenterY=22 CenterZ=0 NormalX=0 NormalY=0 NormalZ=1 Radius=3.46164
  constraints (2):
    c: Radius(g0) = 3.46164
    c: Radius(g1) = 3.46164
FEATURE [PartDesign::Pad] Pad002010
  Length = 3
  Length2 = 100
  Reversed = true
  Sketch = -> Sketch029
  Type = 0
FEATURE [Sketcher::SketchObject] Sketch030
  Placement = pos=(0,0,-13.2) rot=(1,0,0;3.14159rad)
  Support = -> Pad002010 [Face52]
  sketch-geometry (2):
    g0: Circle CenterX=96.5 CenterY=22 CenterZ=0 NormalX=0 NormalY=0 NormalZ=1 Radius=1.8
    g1: Circle CenterX=114.5 CenterY=22 CenterZ=0 NormalX=0 NormalY=0 NormalZ=1 Radius=1.8
  constraints (2):
    c: Radius(g0) = 1.8
    c: Radius(g1) = 1.8
FEATURE [PartDesign::Pocket] Pocket017
  Length = 5
  Sketch = -> Sketch030
  Type = 0
FEATURE [PartDesign::Fillet] Fillet007
  Base = -> Pocket017 [Edge87,Edge31]
  Radius = 2
FEATURE [PartDesign::Fillet] Fillet008
  Base = -> Fillet007 [Edge48]
  Radius = 1
FEATURE [PartDesign::Fillet] Fillet009
  Base = -> Fillet008 [Edge44]
  Radius = 1
FEATURE [Part::Feature] Fillet009001  label="HexagonHotendFanShroud"
  shape: bbox 25.53 x 43.75 x 27.5 mm, 64 faces (baked)
FEATURE [Mesh::Feature] Hotend_Dummy___GTMax3D  label="Hotend_Dummy_-_GTMax3D"
  Placement = pos=(155,-57,-64) rot=(0,0,1;0rad)
FEATURE [Mesh::Feature] ventilador_hotend
  Placement = pos=(106,-61,-43.5) rot=(0,0,1;0rad)
